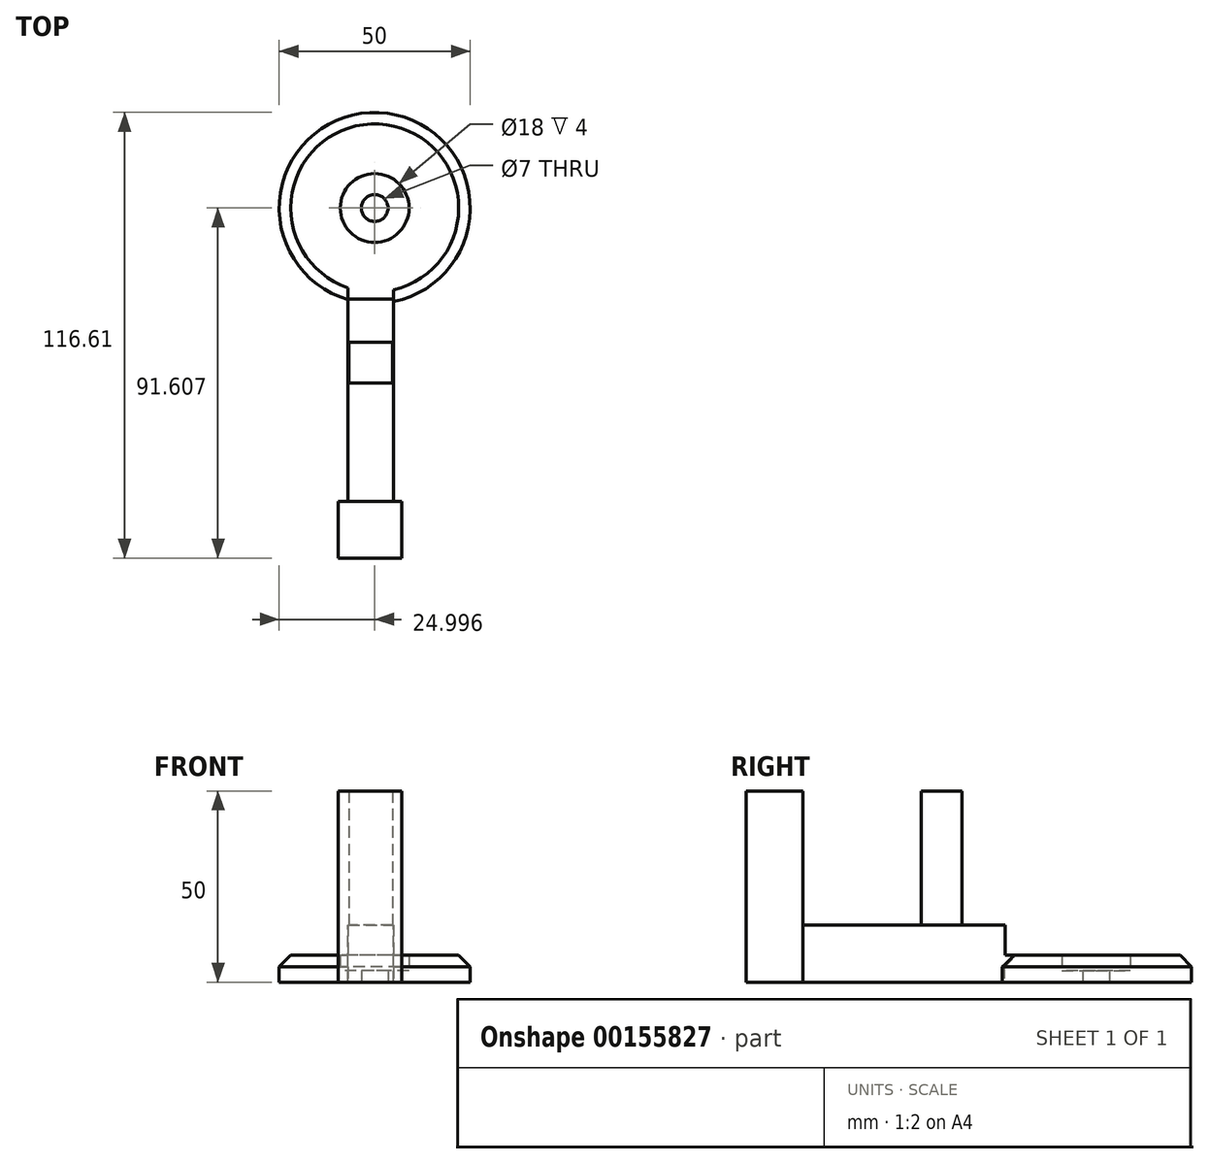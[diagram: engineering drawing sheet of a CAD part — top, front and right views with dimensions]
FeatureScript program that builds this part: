
annotation { "Feature Type Name" : "Feature", "Feature Type Description" : "" }
export const myFeature = defineFeature(function(context is Context, id is Id, definition is map)
    precondition{}
    {
        {
            var Q0;
            Q0=qCreatedBy(makeId("Top.planeOp"),FACE);
            var sketch = newSketch(context, id + "F0", { "sketchPlane" : qUnion([Q0])});
            skCircle(sketch, "E0", {"center": v(-39.23, 27.88) * mm, "radius": 25 * mm});
            skCircle(sketch, "E1", {"center": v(-39.23, 27.88) * mm, "radius": 3.5 * mm});
            skCircle(sketch, "E2", {"center": v(-39.23, 27.88) * mm, "radius": 9 * mm});
            skSolve(sketch);
        }
        {
            var Q0;
            Q0 = qSketchRegion(id + "F0", true);
            extrude(context, id + "F1", {"entities" : qUnion([Q0]), "depth" : 7 * mm});
        }
        {
            var Q0;
            Q0=makeQuery(id+"F0.imprint","IMPRINT",FACE,{"disambiguationData":[TD([[makeQuery(id+"F0.imprint","IMPRINT",EDGE,{"derivedFrom":sQuery(id+"F0.wireOp",EDGE,"E1")}),-1.0]])]});
            extrude(context, id + "F2", {"entities" : qUnion([Q0]), "operationType" : NewBodyOperationType.ADD, "depth" : 3 * mm});
        }
        {
            var Q0;
            Q0=qCreatedBy(makeId("Top.planeOp"),FACE);
            var sketch = newSketch(context, id + "F3", { "sketchPlane" : qUnion([Q0])});
            skLineSegment(sketch, "E3.bottom", {"start": v(-46.18, 4.04) * mm, "end": v(-34.35, 4.04) * mm});
            skLineSegment(sketch, "E3.top", {"start": v(-46.18, -50.78) * mm, "end": v(-34.35, -50.78) * mm});
            skLineSegment(sketch, "E3.left", {"start": v(-46.18, 4.04) * mm, "end": v(-46.18, -50.78) * mm});
            skLineSegment(sketch, "E3.right", {"start": v(-34.35, 4.04) * mm, "end": v(-34.35, -50.78) * mm});
            skSolve(sketch);
        }
        {
            var Q0;
            Q0=makeQuery(id+"F3.imprint","IMPRINT",FACE,{"disambiguationData":[TD([[makeQuery(id+"F3.imprint","IMPRINT",EDGE,{"derivedFrom":sQuery(id+"F3.wireOp",EDGE,"E3.bottom")}),-1.0]])]});
            extrude(context, id + "F4", {"entities" : qUnion([Q0]), "operationType" : NewBodyOperationType.ADD, "depth" : 15 * mm});
        }
        {
            var Q0;
            Q0=qCreatedBy(makeId("Top.planeOp"),FACE);
            var sketch = newSketch(context, id + "F5", { "sketchPlane" : qUnion([Q0])});
            skLineSegment(sketch, "E4.bottom", {"start": v(-46, -7.23) * mm, "end": v(-34.54, -7.23) * mm});
            skLineSegment(sketch, "E4.top", {"start": v(-46, -17.93) * mm, "end": v(-34.54, -17.93) * mm});
            skLineSegment(sketch, "E4.left", {"start": v(-46, -7.23) * mm, "end": v(-46, -17.93) * mm});
            skLineSegment(sketch, "E4.right", {"start": v(-34.54, -7.23) * mm, "end": v(-34.54, -17.93) * mm});
            skSolve(sketch);
        }
        {
            var Q0;
            Q0=qCreatedBy(makeId("Top.planeOp"),FACE);
            var sketch = newSketch(context, id + "F6", { "sketchPlane" : qUnion([Q0])});
            skLineSegment(sketch, "E5.bottom", {"start": v(-48.8, -48.9) * mm, "end": v(-32.1, -48.9) * mm});
            skLineSegment(sketch, "E5.top", {"start": v(-48.8, -63.73) * mm, "end": v(-32.1, -63.73) * mm});
            skLineSegment(sketch, "E5.left", {"start": v(-48.8, -48.9) * mm, "end": v(-48.8, -63.73) * mm});
            skLineSegment(sketch, "E5.right", {"start": v(-32.1, -48.9) * mm, "end": v(-32.1, -63.73) * mm});
            skSolve(sketch);
        }
        {
            var Q0;
            Q0=makeQuery(id+"F1.opExtrude","CAP_EDGE",EDGE,{"disambiguationData":[OSD([sQuery(id+"F0.wireOp",EDGE,"E0")])],"isStart":false});
            chamfer(context, id + "F7", {"entities" : qUnion([Q0]), "width" : 3 * mm, "tangentPropagation" : true});
        }
        {
            var Q0;
            Q0=makeQuery(id+"F6.imprint","IMPRINT",FACE,{"disambiguationData":[TD([[makeQuery(id+"F6.imprint","IMPRINT",EDGE,{"derivedFrom":sQuery(id+"F6.wireOp",EDGE,"E5.bottom")}),-1.0]])]});
            extrude(context, id + "F8", {"entities" : qUnion([Q0]), "operationType" : NewBodyOperationType.ADD, "depth" : 50 * mm});
        }
        {
            var Q0;
            Q0=makeQuery(id+"F5.imprint","IMPRINT",FACE,{"disambiguationData":[TD([[makeQuery(id+"F5.imprint","IMPRINT",EDGE,{"derivedFrom":sQuery(id+"F5.wireOp",EDGE,"E4.bottom")}),-1.0]])]});
            extrude(context, id + "F9", {"entities" : qUnion([Q0]), "operationType" : NewBodyOperationType.ADD, "depth" : 50 * mm});
        }
    });
